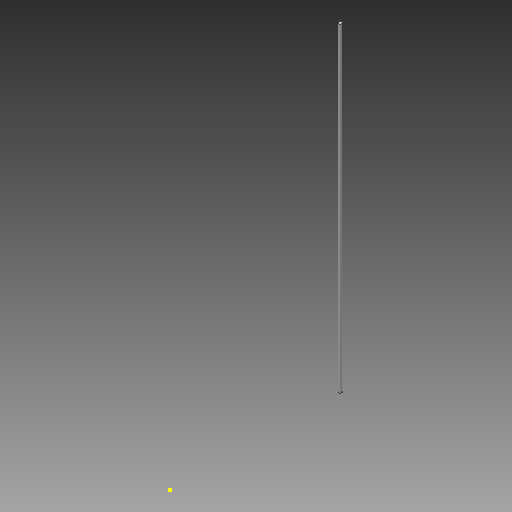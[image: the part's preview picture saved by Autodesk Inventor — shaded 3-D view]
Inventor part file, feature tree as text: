
AUTODESK INVENTOR PART (.ipt)
format: ipt  version: 2018 (Build 220112000, 112)  size: 69,632 bytes
history: native  units: mm
features: other x3, sketch x2
ambient origin geometry x8: Origin, YZ Plane, XZ Plane, XY Plane, X Axis, Y Axis, Z Axis, Center Point
bodies: Solid1 (feature_tree)
feature tree (5):
  other  "Lead Screw-A.ipt"
  other  "Solid1::Lead Screw-A.ipt"
  other  "TaggingFeature1"
  sketch  "Sketch1"  dims[d0=10.0mm]
  sketch  "Sketch2"
